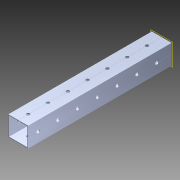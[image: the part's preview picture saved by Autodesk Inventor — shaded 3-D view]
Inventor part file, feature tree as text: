
AUTODESK INVENTOR PART (.ipt)
format: ipt  version: 2014 (Build 180170000, 170)  size: 1,147,392 bytes
history: native  units: in
note: dims shown in document units (in); Inventor stores cm internally (conversion verified against a paired STEP export)
features: pattern_circular x1, other x1, plane x1, extrude x1, imported_body x1, sketch x1
ambient origin geometry x8: Origin, YZ Plane, XZ Plane, XY Plane, X Axis, Y Axis, Z Axis, Center Point
bodies: Body1 (feature_tree)
feature tree (6):
  pattern_circular  "CirPattern2"
  other  "217-3426-STEP1"
  plane  "Work Plane1"
  extrude  "Extrusion1"  Depth=3937.0079in TaperAngle=0.0deg
  imported_body  "Base1"
  sketch  "Sketch1"  dims[d0=-6.125in d1=3937.0079in d2=0.0in]
